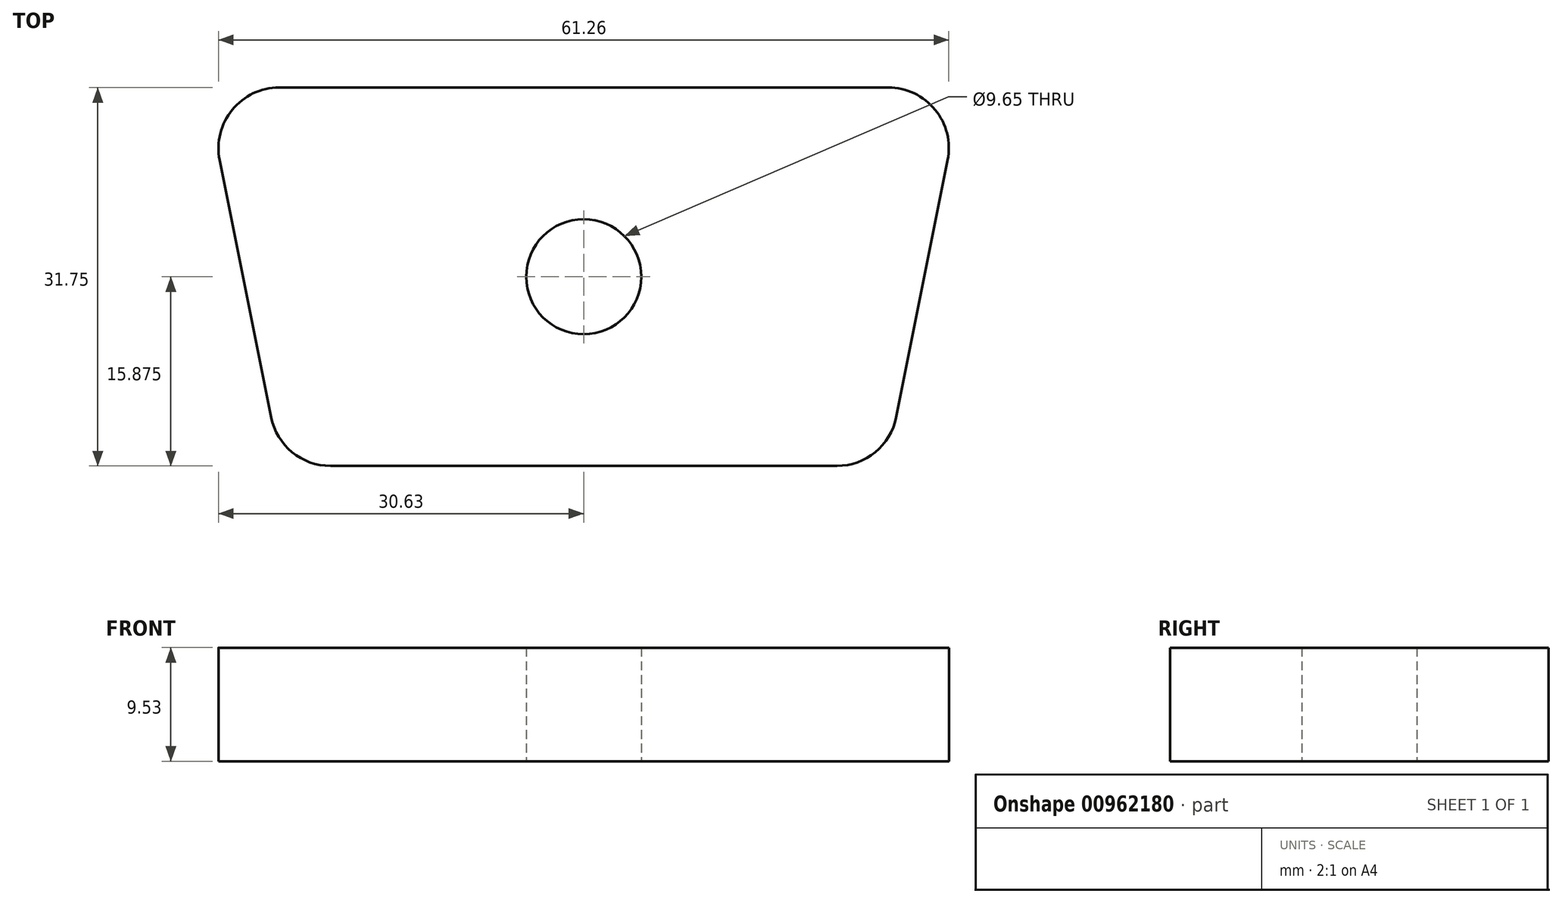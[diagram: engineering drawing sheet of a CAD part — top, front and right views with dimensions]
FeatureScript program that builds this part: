
annotation { "Feature Type Name" : "Feature", "Feature Type Description" : "" }
export const myFeature = defineFeature(function(context is Context, id is Id, definition is map)
    precondition{}
    {
        {
            var Q0;
            Q0=qCreatedBy(makeId("Top.planeOp"),FACE);
            var sketch = newSketch(context, id + "F0", { "sketchPlane" : qUnion([Q0])});
            skLineSegment(sketch, "E0", {"start": v(0, 31.75) * mm, "end": v(-31.75, 31.75) * mm});
            skLineSegment(sketch, "E1", {"start": v(-31.75, 31.75) * mm, "end": v(-25.4, 0) * mm});
            skLineSegment(sketch, "E2", {"start": v(-25.4, 0) * mm, "end": v(0, 0) * mm});
            skLineSegment(sketch, "E3", {"start": v(0, 31.75) * mm, "end": v(31.75, 31.75) * mm});
            skLineSegment(sketch, "E4", {"start": v(31.75, 31.75) * mm, "end": v(25.4, 0) * mm});
            skLineSegment(sketch, "E5", {"start": v(25.4, 0) * mm, "end": v(0, 0) * mm});
            skSolve(sketch);
        }
        {
            var Q0;
            Q0=makeQuery(id+"F0.imprint","IMPRINT",FACE,{"disambiguationData":[TD([[makeQuery(id+"F0.imprint","IMPRINT",EDGE,{"derivedFrom":sQuery(id+"F0.wireOp",EDGE,"E0")}),1.0]])]});
            var sketch = newSketch(context, id + "F1", { "sketchPlane" : qUnion([Q0])});
            skCircle(sketch, "E6", {"center": v(0, 15.88) * mm, "radius": 4.83 * mm});
            skSolve(sketch);
        }
        {
            var Q0;
            Q0=makeQuery(id+"F0.imprint","IMPRINT",FACE,{"disambiguationData":[TD([[makeQuery(id+"F0.imprint","IMPRINT",EDGE,{"derivedFrom":sQuery(id+"F0.wireOp",EDGE,"E0")}),1.0]])]});
            extrude(context, id + "F2", {"entities" : qUnion([Q0]), "depth" : 9.52 * mm, "offsetDistance" : 25.4 * mm});
        }
        {
            var Q0;
            Q0=makeQuery(id+"F1.imprint","IMPRINT",FACE,{"disambiguationData":[TD([[makeQuery(id+"F1.imprint","IMPRINT",EDGE,{"derivedFrom":sQuery(id+"F1.wireOp",EDGE,"E6")}),1.0]])]});
            extrude(context, id + "F3", {"entities" : qUnion([Q0]), "operationType" : NewBodyOperationType.REMOVE, "endBound" : BoundingType.UP_TO_NEXT, "depth" : 19.3 * mm, "offsetDistance" : 25.4 * mm});
        }
        {
            var Q0;
            Q0=makeQuery(id+"F2.opExtrude","SWEPT_EDGE",EDGE,{"disambiguationData":[OSD([sQuery(id+"F0.wireOp",EDGE,"E0"),sQuery(id+"F0.wireOp",EDGE,"E1")])]});
            var Q1;
            Q1=makeQuery(id+"F2.opExtrude","SWEPT_EDGE",EDGE,{"disambiguationData":[OSD([sQuery(id+"F0.wireOp",EDGE,"E3"),sQuery(id+"F0.wireOp",EDGE,"E4")])]});
            var Q2;
            Q2=makeQuery(id+"F2.opExtrude","SWEPT_EDGE",EDGE,{"disambiguationData":[OSD([sQuery(id+"F0.wireOp",EDGE,"E4"),sQuery(id+"F0.wireOp",EDGE,"E5")])]});
            var Q3;
            Q3=makeQuery(id+"F2.opExtrude","SWEPT_EDGE",EDGE,{"disambiguationData":[OSD([sQuery(id+"F0.wireOp",EDGE,"E1"),sQuery(id+"F0.wireOp",EDGE,"E2")])]});
            fillet(context, id + "F4", {"entities" : qUnion([Q0, Q1, Q2, Q3]), "radius" : 5.08 * mm, "tangentPropagation" : true, "allowEdgeOverflow" : false});
        }
    });
